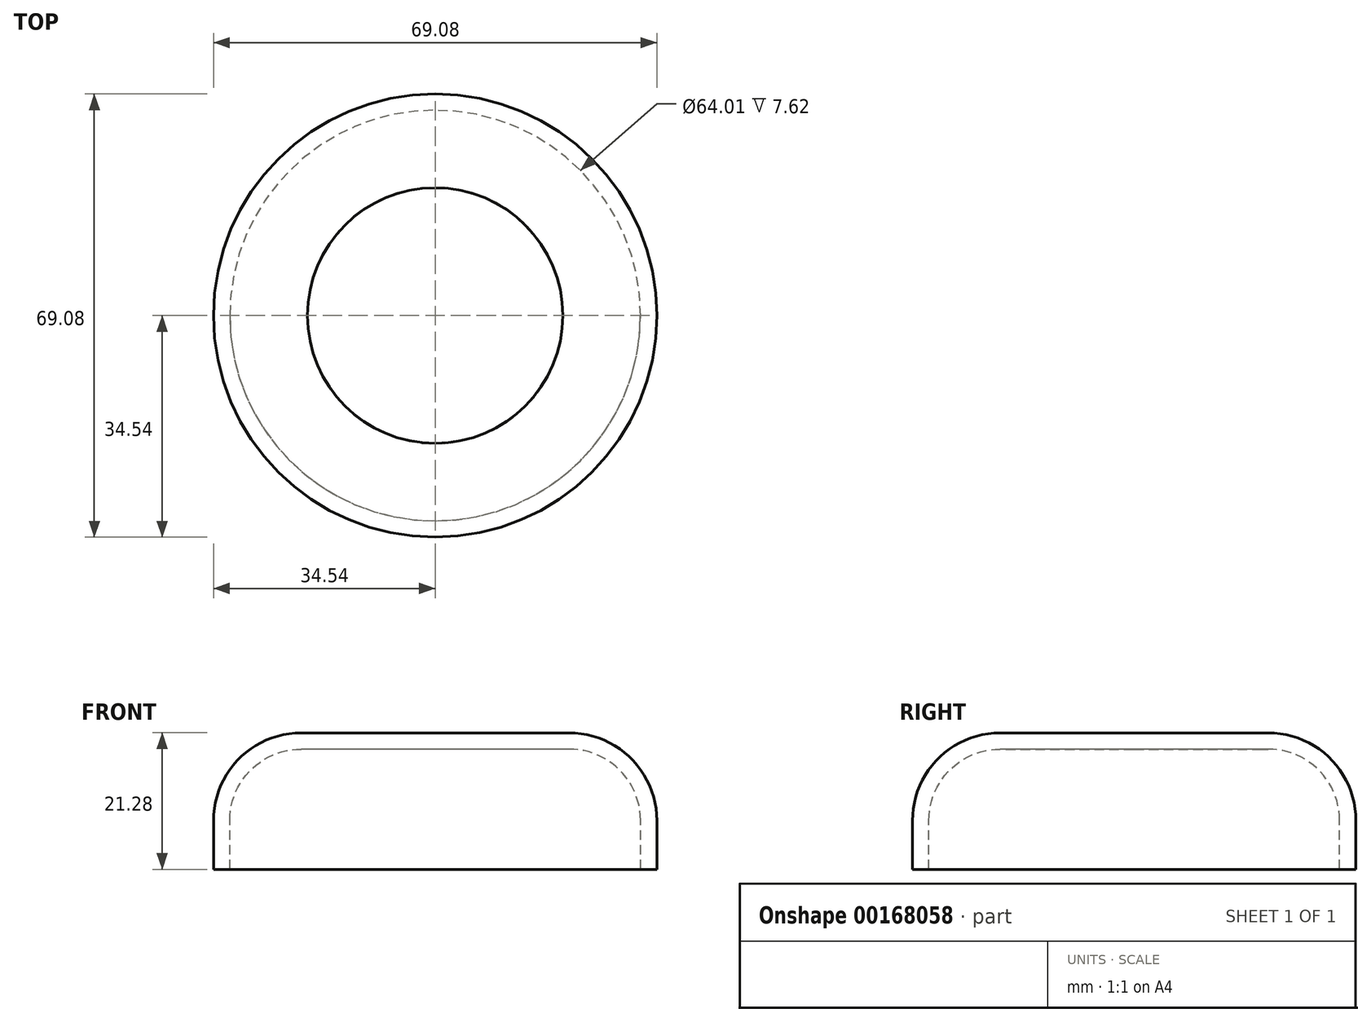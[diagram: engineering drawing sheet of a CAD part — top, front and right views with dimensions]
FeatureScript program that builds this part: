
annotation { "Feature Type Name" : "Feature", "Feature Type Description" : "" }
export const myFeature = defineFeature(function(context is Context, id is Id, definition is map)
    precondition{}
    {
        {
            var Q0;
            Q0=qCreatedBy(makeId("Front.planeOp"),FACE);
            var sketch = newSketch(context, id + "F0", { "sketchPlane" : qUnion([Q0])});
            skLineSegment(sketch, "E0", {"start": v(0, 0) * mm, "end": v(46.35, 0) * mm, "construction": true});
            skLineSegment(sketch, "E1", {"start": v(46.35, 0) * mm, "end": v(46.35, 7.62) * mm, "construction": true});
            skLineSegment(sketch, "E2", {"start": v(19.05, 33.02) * mm, "end": v(19.05, 50.8) * mm, "construction": true});
            skLineSegment(sketch, "E3", {"start": v(19.05, 50.8) * mm, "end": v(0, 50.8) * mm, "construction": true});
            skLineSegment(sketch, "E4", {"start": v(0, 50.8) * mm, "end": v(0, 0) * mm, "construction": true});
            skArc(sketch, "E5", {"start": v(46.35, 7.62) * mm, "mid": v(38.23, 26.27) * mm, "end": v(19.05, 33.02) * mm, "construction": true});
            skArc(sketch, "E6.0", {"start": v(34.54, 7.62) * mm, "mid": v(30.19, 17.62) * mm, "end": v(19.9, 21.24) * mm});
            skLineSegment(sketch, "E6.1", {"start": v(34.54, 0) * mm, "end": v(34.54, 7.62) * mm});
            skLineSegment(sketch, "E7", {"start": v(19.9, 21.24) * mm, "end": v(0, 21.24) * mm});
            skLineSegment(sketch, "E8", {"start": v(0, 21.24) * mm, "end": v(0, 0) * mm});
            skLineSegment(sketch, "E9", {"start": v(34.54, 0) * mm, "end": v(0, 0) * mm});
            skSolve(sketch);
        }
        {
            var Q0;
            Q0=makeQuery(id+"F0.imprint","IMPRINT",FACE,{"disambiguationData":[TD([[makeQuery(id+"F0.imprint","IMPRINT",EDGE,{"derivedFrom":sQuery(id+"F0.wireOp",EDGE,"E6.0")}),1.0]])]});
            var Q1;
            Q1=sQuery(id+"F0.wireOp",EDGE,"E8");
            revolve(context, id + "F1", {"entities" : qUnion([Q0]), "axis" : qUnion([Q1]), "revolveType" : RevolveType.FULL});
        }
        {
            var Q0;
            Q0=makeQuery(id+"F1.opRevolve","SWEPT_FACE",FACE,{"disambiguationData":[OSD([sQuery(id+"F0.wireOp",EDGE,"E9")])]});
            shell(context, id + "F2", {"entities" : qUnion([Q0]), "thickness" : 2.54 * mm});
        }
    });
